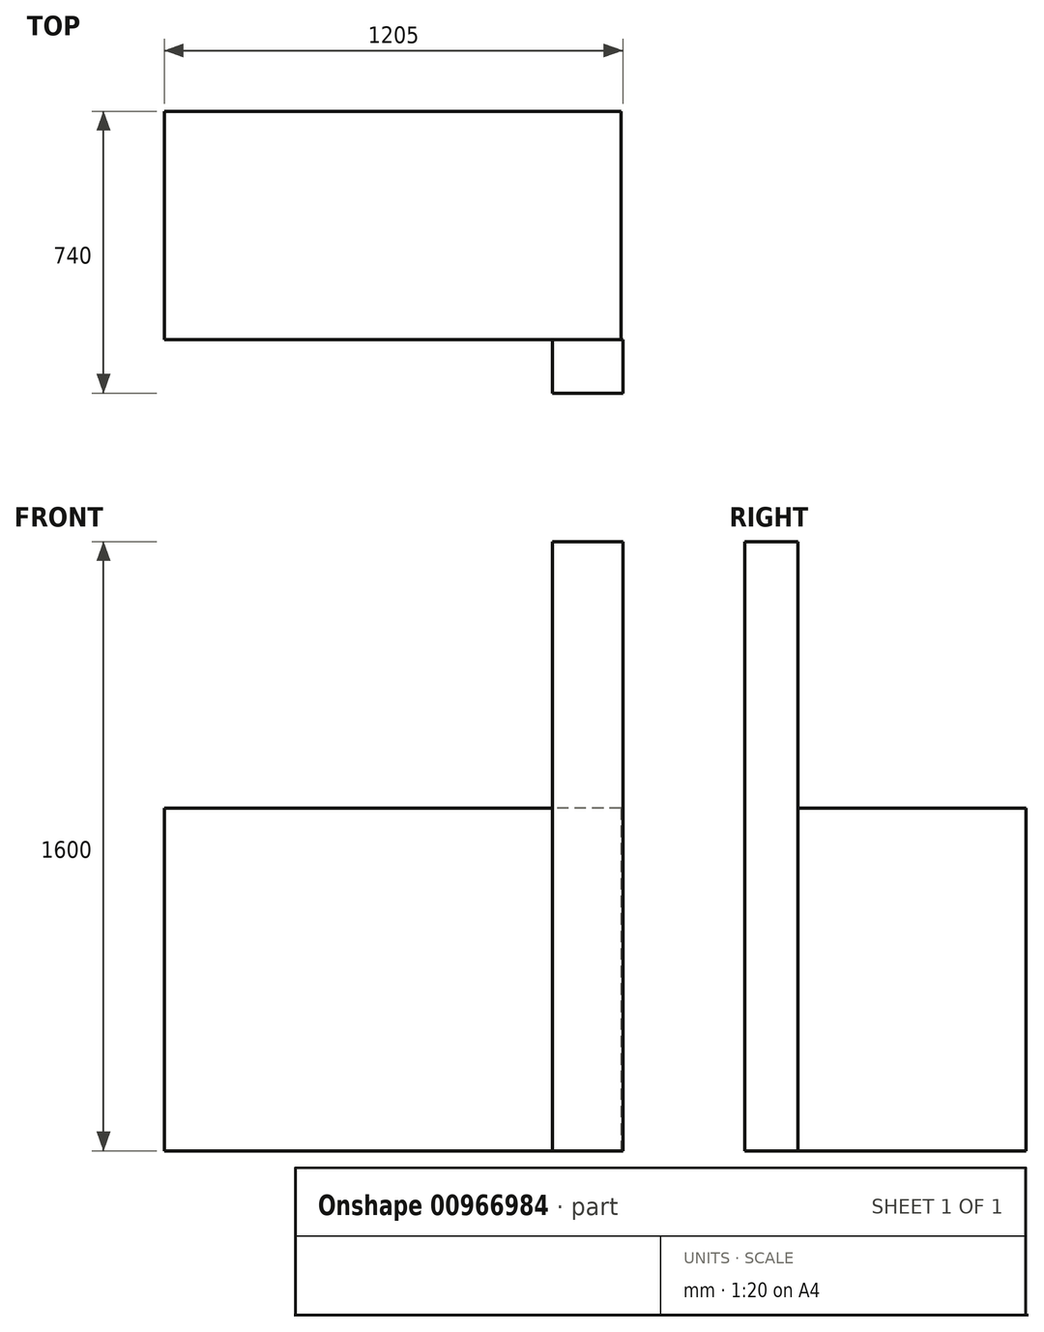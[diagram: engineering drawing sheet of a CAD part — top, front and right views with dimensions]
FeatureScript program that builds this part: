
annotation { "Feature Type Name" : "Feature", "Feature Type Description" : "" }
export const myFeature = defineFeature(function(context is Context, id is Id, definition is map)
    precondition{}
    {
        {
            var Q0;
            Q0=qCreatedBy(makeId("Top.planeOp"),FACE);
            var sketch = newSketch(context, id + "F0", { "sketchPlane" : qUnion([Q0])});
            skLineSegment(sketch, "E0", {"start": v(1200, 0) * mm, "end": v(0, 0) * mm});
            skLineSegment(sketch, "E1", {"start": v(1200, 0) * mm, "end": v(1200, 600) * mm});
            skLineSegment(sketch, "E2", {"start": v(1200, 600) * mm, "end": v(0, 600) * mm});
            skLineSegment(sketch, "E3", {"start": v(0, 600) * mm, "end": v(0, 0) * mm});
            skSolve(sketch);
        }
        {
            var Q0;
            Q0=makeQuery(id+"F0.imprint","IMPRINT",FACE,{"disambiguationData":[TD([[makeQuery(id+"F0.imprint","IMPRINT",EDGE,{"derivedFrom":sQuery(id+"F0.wireOp",EDGE,"E0")}),-1.0]])]});
            extrude(context, id + "F1", {"entities" : qUnion([Q0]), "depth" : 900 * mm, "offsetDistance" : 25 * mm});
        }
        {
            var Q0;
            Q0=qCreatedBy(makeId("Top.planeOp"),FACE);
            var sketch = newSketch(context, id + "F2", { "sketchPlane" : qUnion([Q0])});
            skLineSegment(sketch, "E4", {"start": v(1020, 0) * mm, "end": v(1020, -140) * mm});
            skLineSegment(sketch, "E5", {"start": v(1205, 0) * mm, "end": v(1205, -140) * mm});
            skLineSegment(sketch, "E6", {"start": v(1205, -140) * mm, "end": v(1020, -140) * mm});
            skLineSegment(sketch, "E7", {"start": v(1020, 0) * mm, "end": v(1205, 0) * mm});
            skSolve(sketch);
        }
        {
            var Q0;
            Q0 = qSketchRegion(id + "F2", true);
            extrude(context, id + "F3", {"entities" : qUnion([Q0]), "operationType" : NewBodyOperationType.ADD, "depth" : 1600 * mm, "offsetDistance" : 25 * mm});
        }
    });
